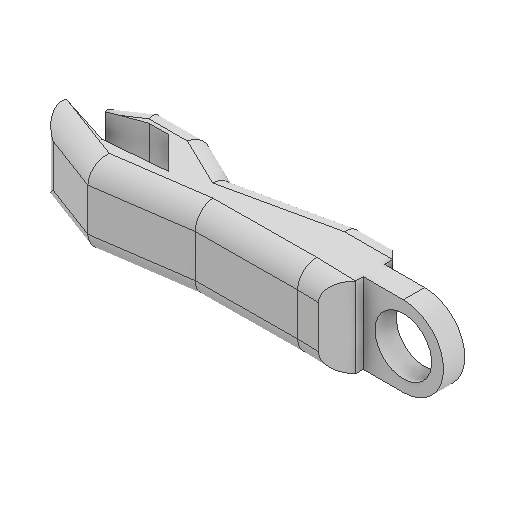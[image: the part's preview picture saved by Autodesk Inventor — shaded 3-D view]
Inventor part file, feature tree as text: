
AUTODESK INVENTOR PART (.ipt)
format: ipt  version: 2022 (Build 260153000, 153)  size: 181,248 bytes
history: native  units: mm
features: sketch x4, other x3
ambient origin geometry x8: Origin, YZ Plane, XZ Plane, XY Plane, X Axis, Y Axis, Z Axis, Center Point
bodies: Solid1 (feature_tree)
feature tree (7):
  other  "lOWER ARM.ipt"
  other  "Solid3::lOWER ARM.ipt"
  other  "TaggingFeature1"
  sketch  "Sketch4"  dims[d0=10.0mm]
  sketch  "Sketch9"
  sketch  "Sketch10"
  sketch  "Sketch11"
